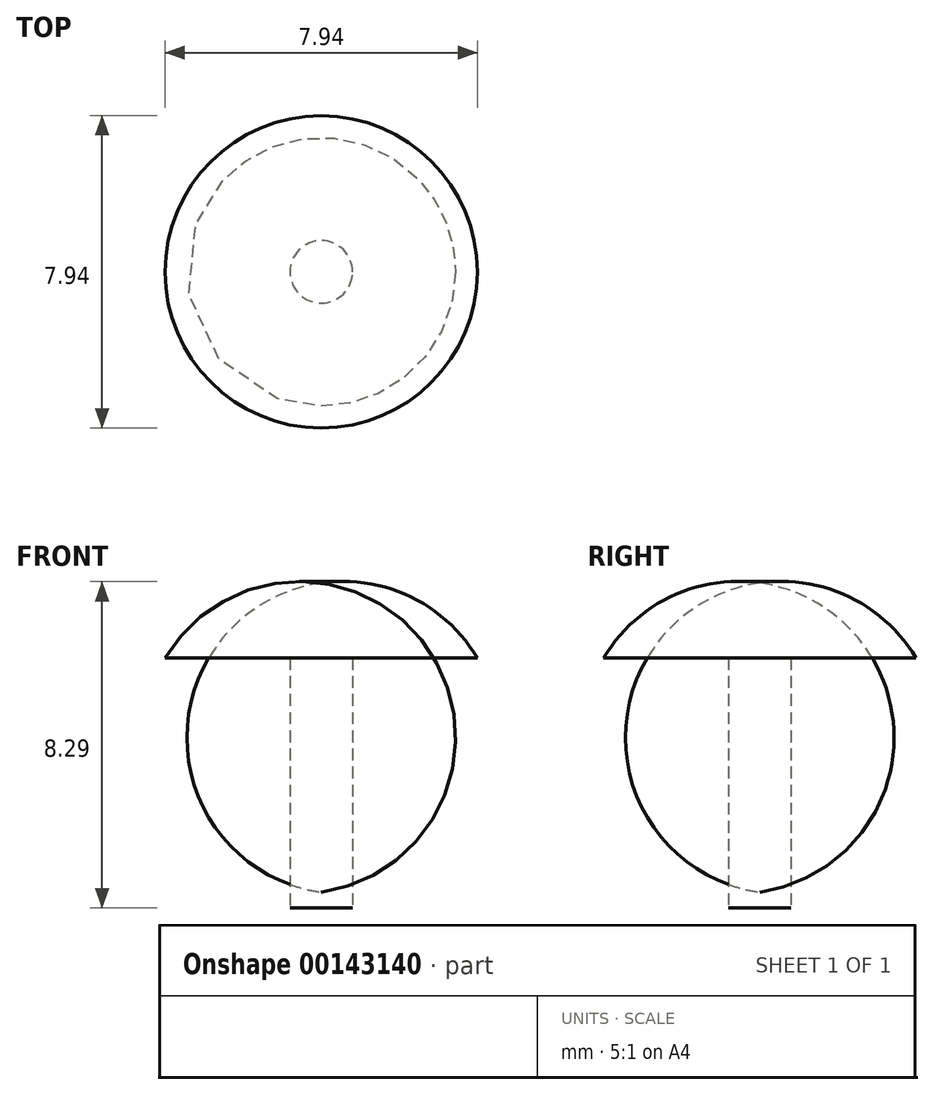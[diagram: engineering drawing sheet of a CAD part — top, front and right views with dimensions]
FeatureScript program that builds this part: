
annotation { "Feature Type Name" : "Feature", "Feature Type Description" : "" }
export const myFeature = defineFeature(function(context is Context, id is Id, definition is map)
    precondition{}
    {
        {
            var Q0;
            Q0=qCreatedBy(makeId("Front.planeOp"),FACE);
            var sketch = newSketch(context, id + "F0", { "sketchPlane" : qUnion([Q0])});
            skLineSegment(sketch, "E0", {"start": v(0, 0) * mm, "end": v(0.8, 0) * mm});
            skLineSegment(sketch, "E1", {"start": v(0.8, 0) * mm, "end": v(0.8, 6.35) * mm});
            skLineSegment(sketch, "E2", {"start": v(0.8, 6.35) * mm, "end": v(3.97, 6.35) * mm});
            skLineSegment(sketch, "E3", {"start": v(0, 0) * mm, "end": v(0, 8.26) * mm});
            skArc(sketch, "E4", {"start": v(3.97, 6.35) * mm, "mid": v(2.27, 7.9) * mm, "end": v(0, 8.26) * mm});
            skSolve(sketch);
        }
        {
            var Q0;
            Q0=makeQuery(id+"F0.imprint","IMPRINT",FACE,{"disambiguationData":[TD([[makeQuery(id+"F0.imprint","IMPRINT",EDGE,{"derivedFrom":sQuery(id+"F0.wireOp",EDGE,"E0")}),1.0]])]});
            var Q1;
            Q1=sQuery(id+"F0.wireOp",EDGE,"E3");
            revolve(context, id + "F1", {"entities" : qUnion([Q0]), "axis" : qUnion([Q1]), "revolveType" : RevolveType.FULL});
        }
    });
